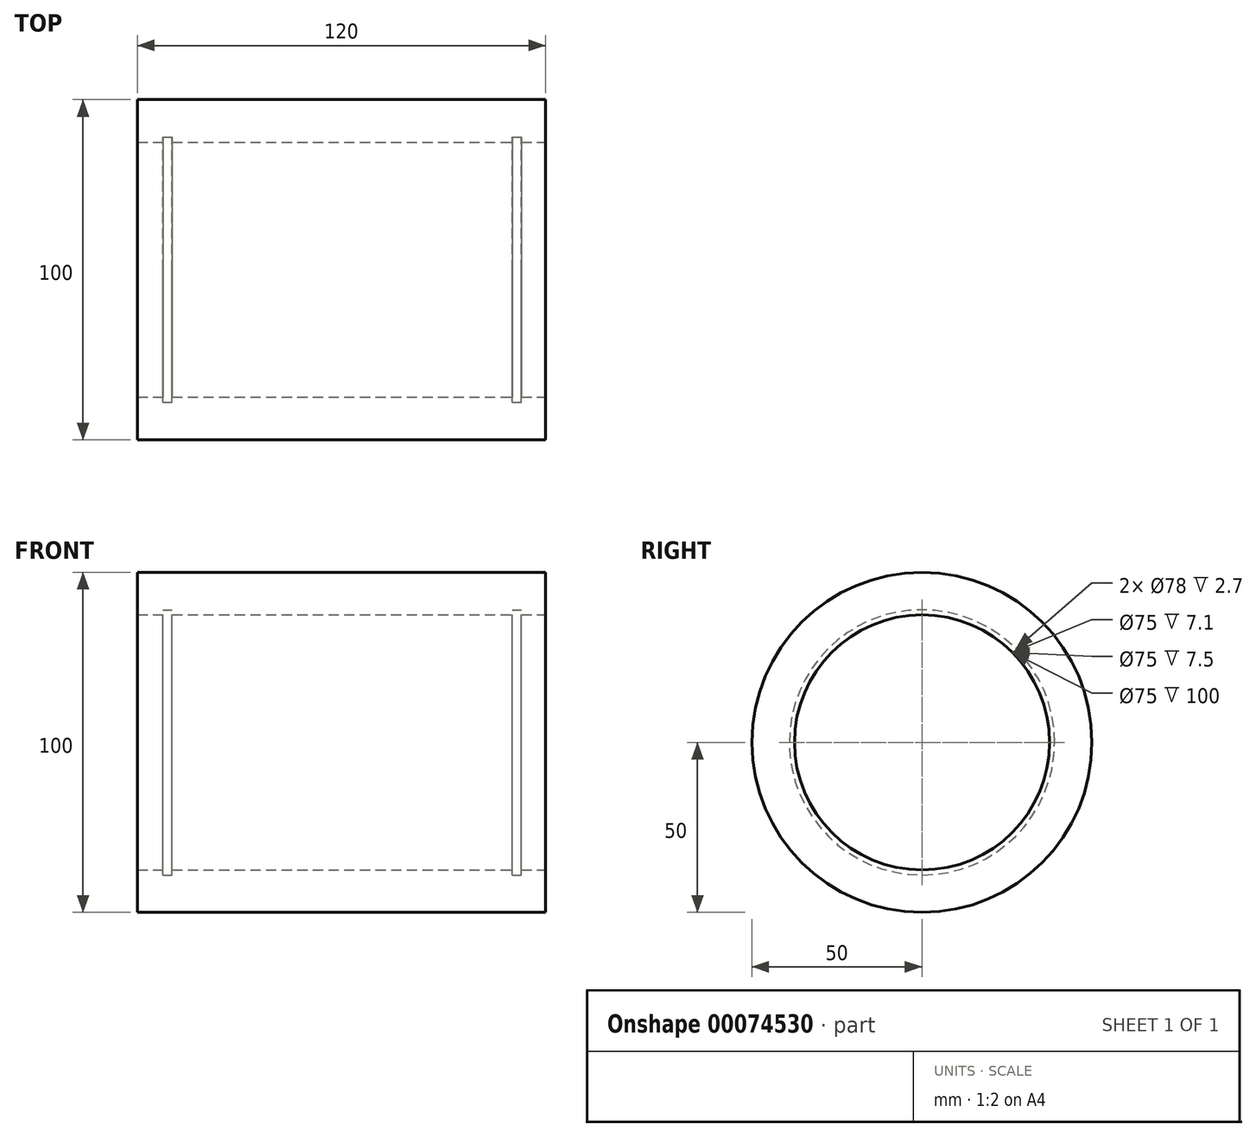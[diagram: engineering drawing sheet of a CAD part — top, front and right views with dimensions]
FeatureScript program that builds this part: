
annotation { "Feature Type Name" : "Feature", "Feature Type Description" : "" }
export const myFeature = defineFeature(function(context is Context, id is Id, definition is map)
    precondition{}
    {
        {
            var Q0;
            Q0=qCreatedBy(makeId("Front.planeOp"),FACE);
            var sketch = newSketch(context, id + "F0", { "sketchPlane" : qUnion([Q0])});
            skLineSegment(sketch, "E0", {"start": v(0, 0) * mm, "end": v(0, 37.5) * mm});
            skLineSegment(sketch, "E1", {"start": v(0, 37.5) * mm, "end": v(7.5, 37.5) * mm});
            skLineSegment(sketch, "E2", {"start": v(7.5, 37.5) * mm, "end": v(7.5, 39) * mm});
            skLineSegment(sketch, "E3", {"start": v(7.5, 39) * mm, "end": v(10.2, 39) * mm});
            skLineSegment(sketch, "E4", {"start": v(10.2, 39) * mm, "end": v(10.2, 37.5) * mm});
            skLineSegment(sketch, "E5", {"start": v(10.2, 37.5) * mm, "end": v(110.2, 37.5) * mm});
            skLineSegment(sketch, "E6", {"start": v(110.2, 37.5) * mm, "end": v(110.2, 39) * mm});
            skLineSegment(sketch, "E7", {"start": v(110.2, 39) * mm, "end": v(112.9, 39) * mm});
            skLineSegment(sketch, "E8", {"start": v(112.9, 39) * mm, "end": v(112.9, 37.5) * mm});
            skLineSegment(sketch, "E9", {"start": v(112.9, 37.5) * mm, "end": v(120, 37.5) * mm});
            skLineSegment(sketch, "E10", {"start": v(120, 37.5) * mm, "end": v(120, 0) * mm});
            skLineSegment(sketch, "E11", {"start": v(120, 0) * mm, "end": v(0, 0) * mm});
            skLineSegment(sketch, "E12", {"start": v(0, 37.5) * mm, "end": v(0, 50) * mm});
            skLineSegment(sketch, "E13", {"start": v(0, 50) * mm, "end": v(120, 50) * mm});
            skLineSegment(sketch, "E14", {"start": v(120, 50) * mm, "end": v(120, 37.5) * mm});
            skSolve(sketch);
        }
        {
            var Q0;
            Q0=makeQuery(id+"F0.imprint","IMPRINT",FACE,{"disambiguationData":[TD([[makeQuery(id+"F0.imprint","IMPRINT",EDGE,{"derivedFrom":sQuery(id+"F0.wireOp",EDGE,"E1")}),1.0]])]});
            var Q1;
            Q1=sQuery(id+"F0.wireOp",EDGE,"E11");
            revolve(context, id + "F1", {"entities" : qUnion([Q0]), "axis" : qUnion([Q1]), "revolveType" : RevolveType.FULL});
        }
    });
